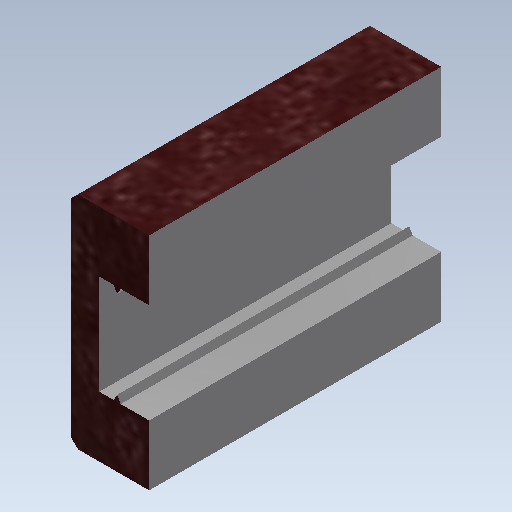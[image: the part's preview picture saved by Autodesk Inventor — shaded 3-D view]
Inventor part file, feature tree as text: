
AUTODESK INVENTOR PART (.ipt)
format: ipt  version: 2021.3 (Build 253353000, 353)  size: 204,288 bytes
history: native  units: mm
features: extrude x4, sketch x4, chamfer x1, reference x1
ambient origin geometry x8: Origin, YZ Plane, XZ Plane, XY Plane, X Axis, Y Axis, Z Axis, Center Point
bodies: Solid1 (feature_tree)
feature tree (10):
  extrude  "Extrusion1"  Depth=31.0mm
  extrude  "Extrusion2"  Depth=7.0mm
  extrude  "Extrusion3"  Depth=41.0mm TaperAngle=0.0deg
  extrude  "Extrusion4"  Depth=1.0mm
  chamfer  "Chamfer1"  Distance=2.0mm
  sketch  "Sketch1"  dims[d0=11.0mm d1=31.0mm]
  sketch  "Sketch2"  dims[d2=41.0mm d3=0.0mm d4=7.0mm]
  sketch  "Sketch3"  dims[d5=14.0mm d6=41.0mm d7=0.0mm]
  reference  "Reference1"
  sketch  "Sketch4"  dims[d8=1.0mm d9=1.0mm d10=2.0mm d11=2.0mm d12=41.0mm d13=0.0mm d14=3.0mm d15=3.0mm d16=11.0mm d17=3.0mm d18=0.0mm d19=1.0mm d20=2.0mm d21=45.0deg]
